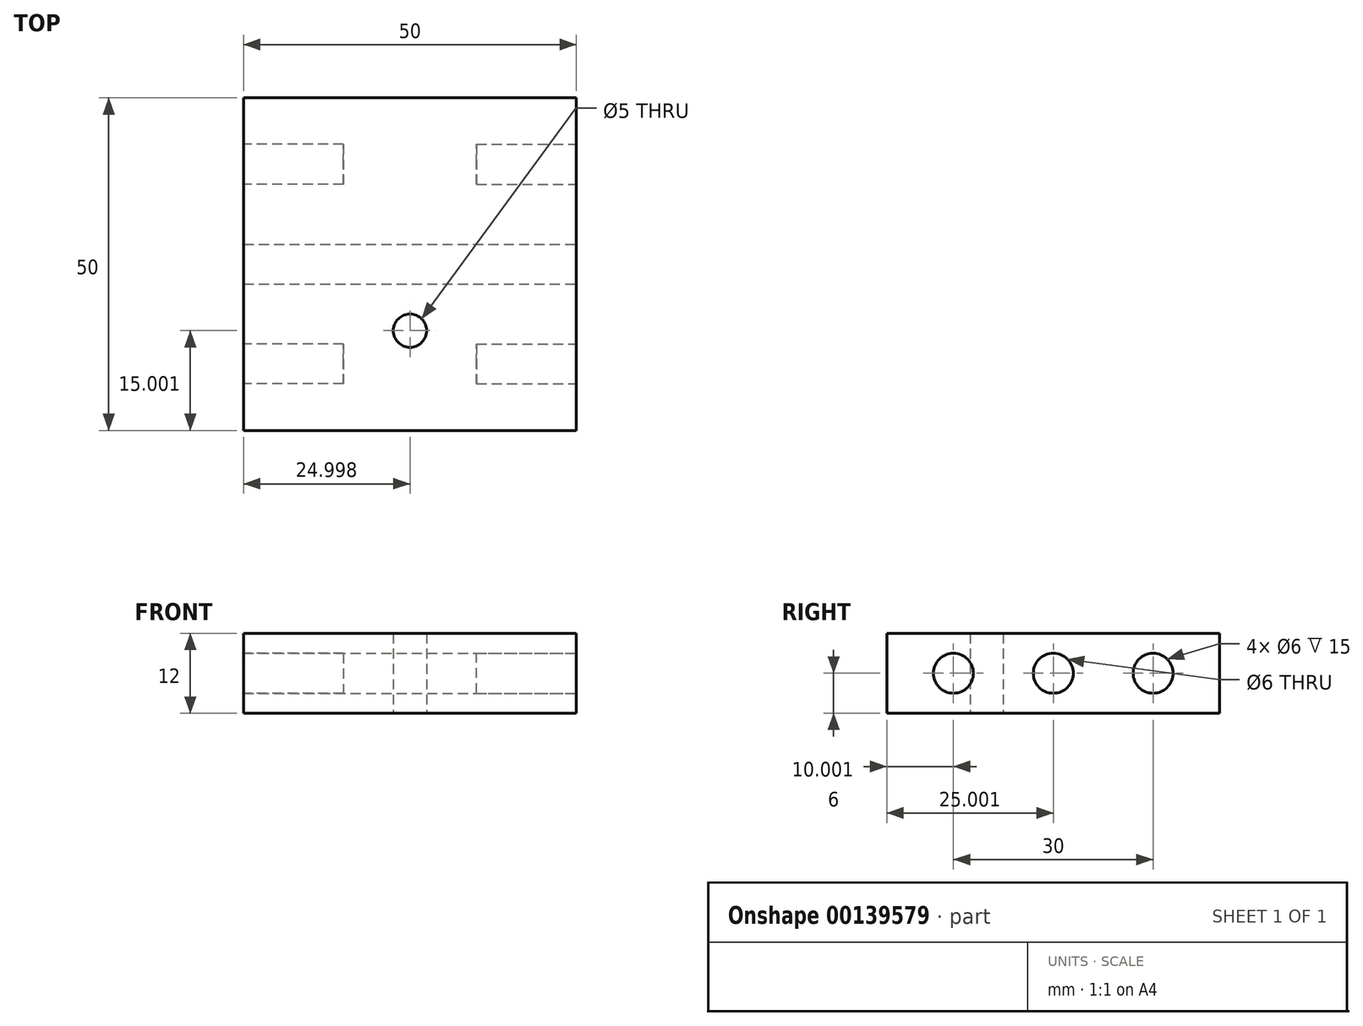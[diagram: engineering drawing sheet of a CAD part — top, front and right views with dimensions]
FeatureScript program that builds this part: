
annotation { "Feature Type Name" : "Feature", "Feature Type Description" : "" }
export const myFeature = defineFeature(function(context is Context, id is Id, definition is map)
    precondition{}
    {
        {
            var Q0;
            Q0=qCreatedBy(makeId("Top.planeOp"),FACE);
            var sketch = newSketch(context, id + "F0", { "sketchPlane" : qUnion([Q0])});
            skLineSegment(sketch, "E0.bottom", {"start": v(-30.5, 20.43) * mm, "end": v(19.5, 20.43) * mm});
            skLineSegment(sketch, "E0.top", {"start": v(-30.5, -29.57) * mm, "end": v(19.5, -29.57) * mm});
            skLineSegment(sketch, "E0.left", {"start": v(-30.5, 20.43) * mm, "end": v(-30.5, -29.57) * mm});
            skLineSegment(sketch, "E0.right", {"start": v(19.5, 20.43) * mm, "end": v(19.5, -29.57) * mm});
            skSolve(sketch);
        }
        {
            var Q0;
            Q0=qSketchRegion(id+"F0",true);
            extrude(context, id + "F1", {"entities" : qUnion([Q0]), "depth" : 12 * mm});
        }
        {
            var Q0;
            Q0=makeQuery(id+"F1.opExtrude","SWEPT_FACE",FACE,{"disambiguationData":[OSD([sQuery(id+"F0.wireOp",EDGE,"E0.left")])]});
            var sketch = newSketch(context, id + "F2", { "sketchPlane" : qUnion([Q0])});
            skCircle(sketch, "E1", {"center": v(-10.43, 6) * mm, "radius": 3 * mm});
            skCircle(sketch, "E2", {"center": v(19.57, 6) * mm, "radius": 3 * mm});
            skSolve(sketch);
        }
        {
            var Q0;
            Q0=makeQuery(id+"F2.imprint","IMPRINT",FACE,{"disambiguationData":[TD([[makeQuery(id+"F2.imprint","IMPRINT",EDGE,{"derivedFrom":sQuery(id+"F2.wireOp",EDGE,"E1")}),1.0]])]});
            var Q1;
            Q1=makeQuery(id+"F2.imprint","IMPRINT",FACE,{"disambiguationData":[TD([[makeQuery(id+"F2.imprint","IMPRINT",EDGE,{"derivedFrom":sQuery(id+"F2.wireOp",EDGE,"E2")}),1.0]])]});
            extrude(context, id + "F3", {"entities" : qUnion([Q0, Q1]), "operationType" : NewBodyOperationType.REMOVE, "oppositeDirection" : true, "depth" : 15 * mm});
        }
        {
            var Q0;
            Q0=makeQuery(id+"F1.opExtrude","SWEPT_FACE",FACE,{"disambiguationData":[OSD([sQuery(id+"F0.wireOp",EDGE,"E0.right")])]});
            var sketch = newSketch(context, id + "F4", { "sketchPlane" : qUnion([Q0])});
            skCircle(sketch, "E3", {"center": v(10.43, 6) * mm, "radius": 3 * mm});
            skCircle(sketch, "E4", {"center": v(-19.57, 6) * mm, "radius": 3 * mm});
            skSolve(sketch);
        }
        {
            var Q0;
            Q0=makeQuery(id+"F4.imprint","IMPRINT",FACE,{"disambiguationData":[TD([[makeQuery(id+"F4.imprint","IMPRINT",EDGE,{"derivedFrom":sQuery(id+"F4.wireOp",EDGE,"E3")}),1.0]])]});
            var Q1;
            Q1=makeQuery(id+"F4.imprint","IMPRINT",FACE,{"disambiguationData":[TD([[makeQuery(id+"F4.imprint","IMPRINT",EDGE,{"derivedFrom":sQuery(id+"F4.wireOp",EDGE,"E4")}),1.0]])]});
            extrude(context, id + "F5", {"entities" : qUnion([Q0, Q1]), "operationType" : NewBodyOperationType.REMOVE, "oppositeDirection" : true, "depth" : 15 * mm});
        }
        {
            var Q0;
            Q0=makeQuery(id+"F1.opExtrude","SWEPT_FACE",FACE,{"disambiguationData":[OSD([sQuery(id+"F0.wireOp",EDGE,"E0.right")])]});
            var sketch = newSketch(context, id + "F6", { "sketchPlane" : qUnion([Q0])});
            skCircle(sketch, "E5", {"center": v(-4.57, 6) * mm, "radius": 3 * mm});
            skSolve(sketch);
        }
        {
            var Q0;
            Q0=makeQuery(id+"F6.imprint","IMPRINT",FACE,{"disambiguationData":[TD([[makeQuery(id+"F6.imprint","IMPRINT",EDGE,{"derivedFrom":sQuery(id+"F6.wireOp",EDGE,"E5")}),1.0]])]});
            extrude(context, id + "F7", {"entities" : qUnion([Q0]), "operationType" : NewBodyOperationType.REMOVE, "endBound" : BoundingType.THROUGH_ALL, "oppositeDirection" : true, "depth" : 25 * mm});
        }
        {
            var Q0;
            Q0=makeQuery(id+"F1.opExtrude","CAP_FACE",FACE,{"disambiguationData":[OSD([sQuery(id+"F0.wireOp",EDGE,"E0.bottom"),sQuery(id+"F0.wireOp",EDGE,"E0.top"),sQuery(id+"F0.wireOp",EDGE,"E0.left"),sQuery(id+"F0.wireOp",EDGE,"E0.right")])],"isStart":true});
            var sketch = newSketch(context, id + "F8", { "sketchPlane" : qUnion([Q0])});
            skCircle(sketch, "E6", {"center": v(-5.5, 14.57) * mm, "radius": 2.5 * mm});
            skSolve(sketch);
        }
        {
            var Q0;
            Q0=makeQuery(id+"F8.imprint","IMPRINT",FACE,{"disambiguationData":[TD([[makeQuery(id+"F8.imprint","IMPRINT",EDGE,{"derivedFrom":sQuery(id+"F8.wireOp",EDGE,"E6")}),1.0]])]});
            extrude(context, id + "F9", {"entities" : qUnion([Q0]), "operationType" : NewBodyOperationType.REMOVE, "endBound" : BoundingType.THROUGH_ALL, "oppositeDirection" : true, "depth" : 25 * mm});
        }
    });
